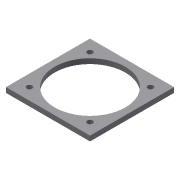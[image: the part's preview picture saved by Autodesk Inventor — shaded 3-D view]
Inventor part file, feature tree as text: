
AUTODESK INVENTOR PART (.ipt)
format: ipt  version: 2013 (Build 170138000, 138)  size: 93,696 bytes
history: native  units: in
note: dims shown in document units (in); Inventor stores cm internally (conversion verified against a paired STEP export)
features: sketch x3, extrude x2, hole x1
ambient origin geometry x8: Origin, YZ Plane, XZ Plane, XY Plane, X Axis, Y Axis, Z Axis, Center Point
feature tree (6):
  extrude  "Extrusion4"  Depth=1.9685in
  extrude  "Extrusion5"  Depth=0.1181in TaperAngle=0.0deg
  hole  "Hole2"  [1 undecoded]
  sketch  "Sketch7"  dims[d5=1.9in d18=1.6in d54=1.9685in]
  sketch  "Sketch8"  dims[d55=1.9685in d56=0.1181in d57=0.0in]
  sketch  "Sketch10"  dims[d58=1.6535in d59=0.1181in d60=0.0in d62=1.4173in d63=1.4173in d64=0.1285in d65=0.2362in d66=0.1575in d67=0.0787in d68=90.0deg d69=0.315in d70=0.8108in]
note: 1 required parameter value undecoded (feature->parameter linkage not recoverable at this tier; creation-order binding heuristic only, values carry confidence <= 0.55)
